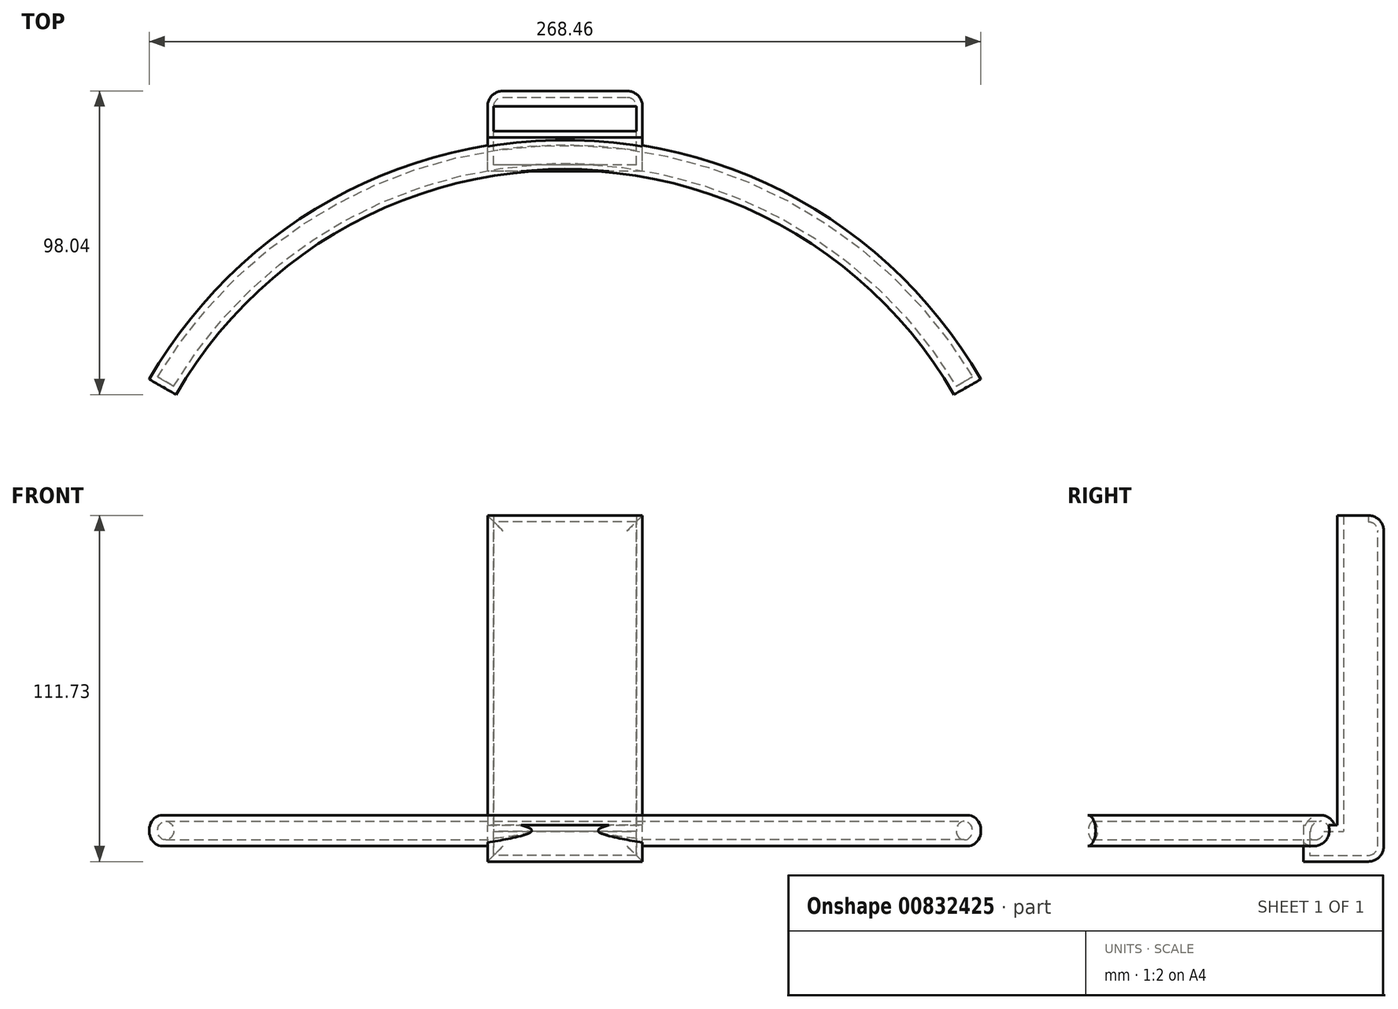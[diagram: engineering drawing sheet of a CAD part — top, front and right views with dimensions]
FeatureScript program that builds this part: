
annotation { "Feature Type Name" : "Feature", "Feature Type Description" : "" }
export const myFeature = defineFeature(function(context is Context, id is Id, definition is map)
    precondition{}
    {
        {
            var Q0;
            Q0=qCreatedBy(makeId("Right.planeOp"),FACE);
            var sketch = newSketch(context, id + "F0", { "sketchPlane" : qUnion([Q0])});
            skCircle(sketch, "E0", {"center": v(30.39, 0) * mm, "radius": 5 * mm});
            skLineSegment(sketch, "E1", {"start": v(-119.61, 22.7) * mm, "end": v(-119.61, -55.44) * mm});
            skSolve(sketch);
        }
        {
            var Q0;
            Q0=makeQuery(id+"F0.imprint","IMPRINT",FACE,{"disambiguationData":[TD([[makeQuery(id+"F0.imprint","IMPRINT",EDGE,{"derivedFrom":sQuery(id+"F0.wireOp",EDGE,"E0")}),1.0]])]});
            var Q1;
            Q1=sQuery(id+"F0.wireOp",EDGE,"E1");
            revolve(context, id + "F1", {"surfaceOperationType" : NewSurfaceOperationType.NEW, "entities" : qUnion([Q0]), "axis" : qUnion([Q1]), "revolveType" : RevolveType.SYMMETRIC, "angle" : 120 * degree});
        }
        {
            var Q0;
            Q0=qCreatedBy(makeId("Right.planeOp"),FACE);
            var sketch = newSketch(context, id + "F2", { "sketchPlane" : qUnion([Q0])});
            skLineSegment(sketch, "E2.bottom", {"start": v(25, 1.73) * mm, "end": v(50.93, 1.73) * mm});
            skLineSegment(sketch, "E2.top", {"start": v(25, -10) * mm, "end": v(50.93, -10) * mm});
            skLineSegment(sketch, "E2.left", {"start": v(25, 1.73) * mm, "end": v(25, -10) * mm});
            skLineSegment(sketch, "E2.right", {"start": v(50.93, 1.73) * mm, "end": v(50.93, -10) * mm});
            skSolve(sketch);
        }
        {
            var Q0;
            Q0=makeQuery(id+"F2.imprint","IMPRINT",FACE,{"disambiguationData":[TD([[makeQuery(id+"F2.imprint","IMPRINT",EDGE,{"derivedFrom":sQuery(id+"F2.wireOp",EDGE,"E2.bottom")}),-1.0]])]});
            extrude(context, id + "F3", {"entities" : qUnion([Q0]), "operationType" : NewBodyOperationType.ADD, "depth" : 25 * mm, "offsetDistance" : 25 * mm, "hasSecondDirection" : true, "secondDirectionOppositeDirection" : true, "secondDirectionDepth" : 25 * mm});
        }
        {
            var Q0;
            {var subQ0=sQuery(id+"F2.wireOp",EDGE,"E2.right");var subQ3=sQuery(id+"F2.wireOp",EDGE,"E2.bottom");Q0=makeQuery(id+"F3.boolean.opBoolean","SPLIT",FACE,{"disambiguationData":[TD([makeQuery(id+"F3.opExtrude","SWEPT_FACE",FACE,{"disambiguationData":[OSD([subQ0])]})])],"derivedFrom":makeQuery(id+"F3.opExtrude","SWEPT_FACE",FACE,{"disambiguationData":[OSD([subQ3])]})});}
            var sketch = newSketch(context, id + "F4", { "sketchPlane" : qUnion([Q0])});
            skLineSegment(sketch, "E3.bottom", {"start": v(-25, 50.93) * mm, "end": v(25, 50.93) * mm});
            skLineSegment(sketch, "E3.top", {"start": v(-25, 35.93) * mm, "end": v(25, 35.93) * mm});
            skLineSegment(sketch, "E3.left", {"start": v(-25, 50.93) * mm, "end": v(-25, 35.93) * mm});
            skLineSegment(sketch, "E3.right", {"start": v(25, 50.93) * mm, "end": v(25, 35.93) * mm});
            skSolve(sketch);
        }
        {
            var Q0;
            Q0 = qSketchRegion(id + "F4", true);
            extrude(context, id + "F5", {"entities" : qUnion([Q0]), "operationType" : NewBodyOperationType.ADD, "depth" : 100 * mm, "offsetDistance" : 25 * mm});
        }
        {
            var Q0;
            Q0=makeQuery(id+"F5.boolean.opBoolean","MERGE",FACE,{"derivedFrom":[makeQuery(id+"F3.opExtrude","SWEPT_FACE",FACE,{"disambiguationData":[OSD([sQuery(id+"F2.wireOp",EDGE,"E2.right")])]}),makeQuery(id+"F5.opExtrude","SWEPT_FACE",FACE,{"disambiguationData":[OSD([sQuery(id+"F4.wireOp",EDGE,"E3.bottom")])]})]});
            fillet(context, id + "F6", {"entities" : qUnion([Q0]), "radius" : 5 * mm, "tangentPropagation" : true, "allowEdgeOverflow" : false});
        }
        {
            var Q0;
            Q0=makeQuery(id+"F5.opExtrude","CAP_FACE",FACE,{"disambiguationData":[OSD([sQuery(id+"F4.wireOp",EDGE,"E3.bottom"),sQuery(id+"F4.wireOp",EDGE,"E3.top"),sQuery(id+"F4.wireOp",EDGE,"E3.left"),sQuery(id+"F4.wireOp",EDGE,"E3.right")])],"isStart":false});
            shell(context, id + "F7", {"entities" : qUnion([Q0]), "thickness" : 2 * mm});
        }
    });
